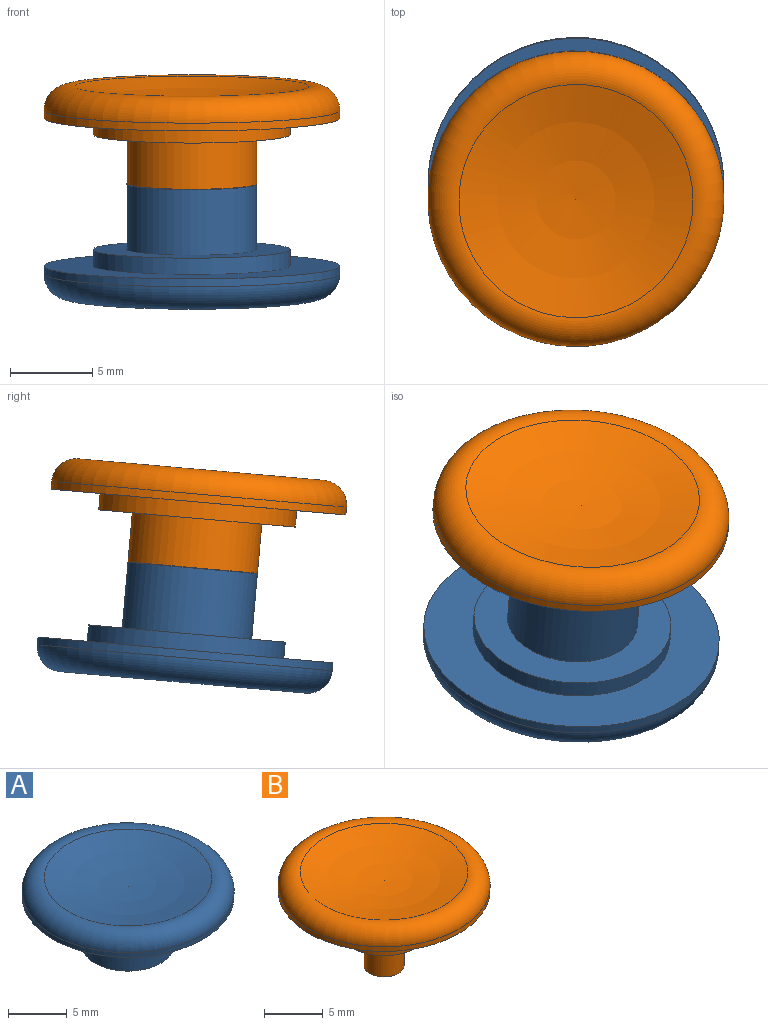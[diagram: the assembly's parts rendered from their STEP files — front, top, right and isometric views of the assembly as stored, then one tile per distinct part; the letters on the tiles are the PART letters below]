
ASSEMBLY  parts=2 mates=1
PART A: 10 faces, bbox 19.5x19.5x7 mm
  f0: cylinder r=1.75mm len=4mm, axis (0,0,-1), area 44mm2, adj f2,f5
  f1: cylinder r=3.95mm len=7.9mm, axis (0,0,-1), area 99.3mm2, adj f2,f3
  f2: plane 7.9x7.9mm, normal (0,0,-1), area 39.4mm2, adj f0,f1
  f3: plane 12x12mm, normal (0,0,-1), area 64.1mm2, adj f1,f4
  f4: cylinder r=6mm len=12mm, axis (0,0,-1), area 37.7mm2, adj f3,f6
  f5: plane 3.5x3.5mm, normal (0,0,-1), area 9.6mm2, adj f0
  f6: plane 18x18mm, normal (0,0,-1), area 141.4mm2, adj f4,f7
  f7: cylinder r=9mm len=18mm, axis (0,0,1), area 27mm2, adj f6,f9
  f8: sphere r=27.75mm, area 161.8mm2, adj f9
  f9: torus R=7.5mm, axis (0,0,1), area 143mm2, adj f7,f8
PART B: 10 faces, bbox 19.5x19.5x9.8 mm
  f0: cylinder r=3.95mm len=7.9mm, axis (0,0,-1), area 74.5mm2, adj f1,f3
  f1: plane 7.9x7.9mm, normal (0,0,-1), area 39.9mm2, adj f0,f8
  f2: cylinder r=6mm len=12mm, axis (0,0,-1), area 37.7mm2, adj f3,f4
  f3: plane 12x12mm, normal (0,0,-1), area 64.1mm2, adj f0,f2
  f4: plane 18x18mm, normal (0,0,-1), area 141.4mm2, adj f2,f5
  f5: cylinder r=9mm len=18mm, axis (0,0,1), area 27mm2, adj f4,f7
  f6: sphere r=27.75mm, area 161.8mm2, adj f7
  f7: torus R=7.5mm, axis (0,0,1), area 143mm2, adj f5,f6
  f8: cylinder r=1.7mm len=3.8mm, axis (0,0,1), area 40.6mm2, adj f1,f9
  f9: plane 3.4x3.4mm, normal (0,0,-1), area 9.1mm2, adj f8
PLACE A rot(axis=(-1,0,0),175deg) t=(-8.7,10.51,26.59)mm
PLACE B rot(axis=(1,0,0),5deg) t=(-8.7,10.51,26.62)mm
MATE cylindrical A.f0 <-> B.f8  axis (0,-0.09,1) through (-8.7,10.51,26.59)mm
